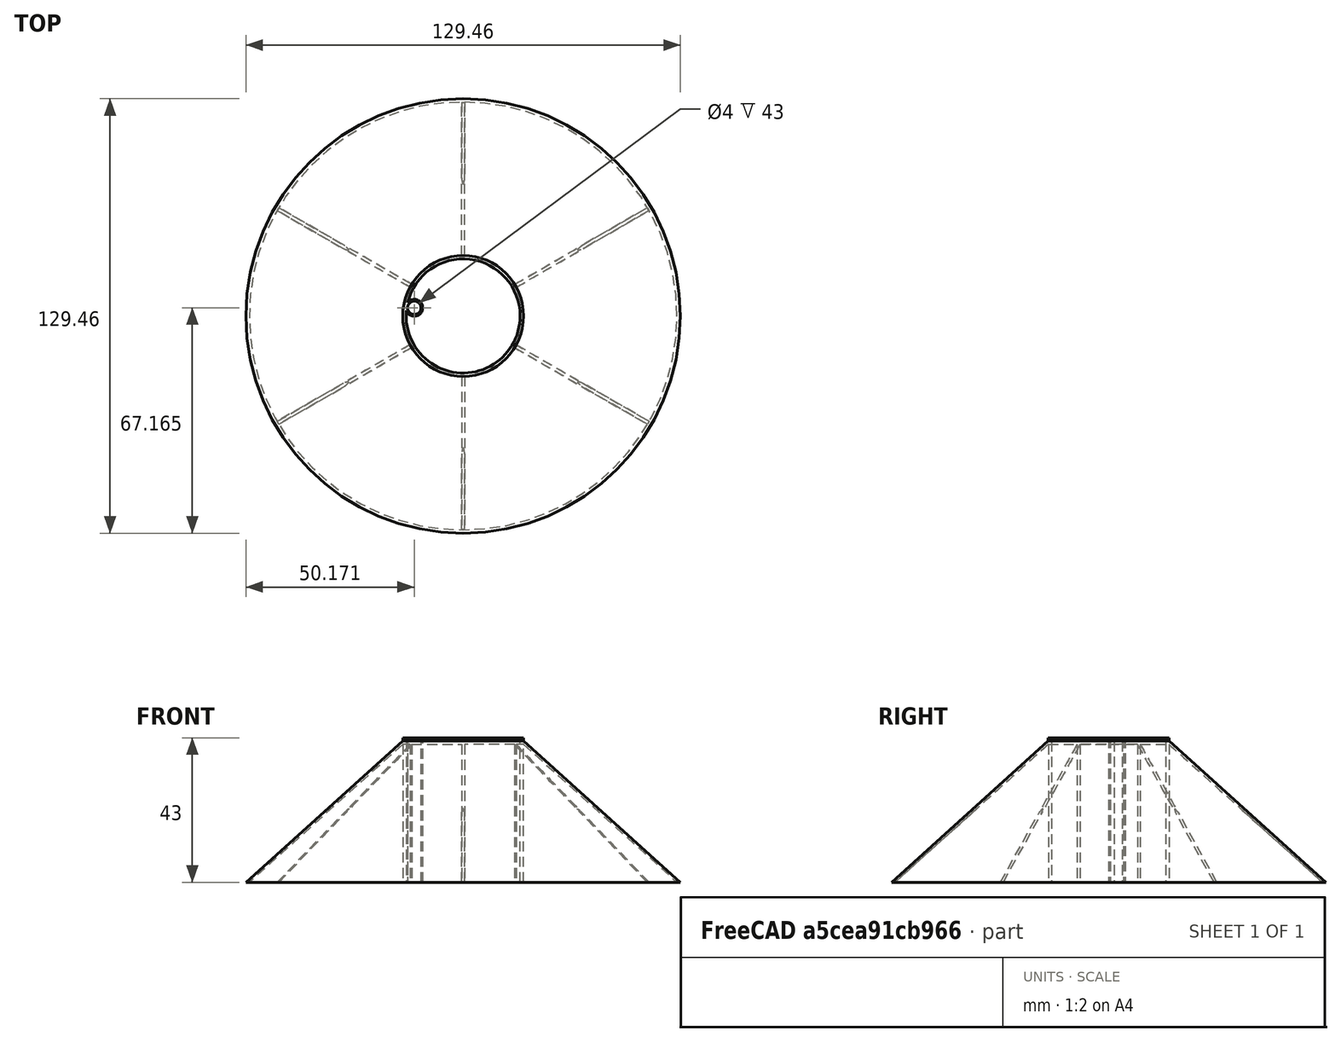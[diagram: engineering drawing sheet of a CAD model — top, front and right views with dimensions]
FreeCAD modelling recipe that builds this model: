
FCSTD DOCUMENT  (FreeCAD 0.20R29603 (Git))
Label: Ez3D-Mini-SaucerX3
License: All rights reserved
LicenseURL: http://en.wikipedia.org/wiki/All_rights_reserved
objects: Sketcher::SketchObject×4, Mesh::Feature×3, PartDesign::Pad×3, PartDesign::PolarPattern×1, PartDesign::Revolution×1, PartDesign::Body×1
note: 14 computed .brp shape members not serialized (recipe doc carries the construction recipe); baked Part::Feature solids carry a one-line shape summary decoded from their .brp

FEATURE [Mesh::Feature] Ez3D_13mmMotorTubeOnly_Body  label="Ez3D-13mmMotorTubeOnly-Body"
  Placement = pos=(-7.5,-5,0) rot=(0,0,1;0rad)
FEATURE [Mesh::Feature] Ez3D_13mmMotorTubeOnly_Body001  label="Ez3D-13mmMotorTubeOnly-Body001"
  Placement = pos=(7.5,-5,0) rot=(0,0,1;0rad)
FEATURE [Sketcher::SketchObject] Sketch  label="Center Support Structure"
  FullyConstrained = true
  MapMode = 5
  Support = -> [XY_Plane]
  sketch-geometry (2):
    g0: Circle CenterX=0 CenterY=0 CenterZ=0 NormalX=0 NormalY=0 NormalZ=1 AngleXU=0 Radius=17
    g1: Circle CenterX=0 CenterY=0 CenterZ=0 NormalX=0 NormalY=0 NormalZ=1 AngleXU=0 Radius=18
  constraints (4):
    c: Coincident(g0,g-1)
    c: Coincident(g1,g0)
    c: Diameter(g0) = 34
    c: Diameter(g1) = 36
FEATURE [PartDesign::Pad] Pad
  Direction = (0,0,1)
  Length = 43
  Length2 = 10
  Profile = -> Sketch
  ReferenceAxis = -> Sketch [N_Axis]
  Type = 0
FEATURE [Sketcher::SketchObject] Sketch001  label=""Fins""
  FullyConstrained = false
  MapMode = 5
  Placement = pos=(0,0,0) rot=(0.57735,0.57735,0.57735;2.0944rad)
  Support = -> [YZ_Plane]
  sketch-geometry (3):
    g0: LineSegment StartX=17 StartY=42 StartZ=0 EndX=17 EndY=0 EndZ=0
    g1: LineSegment StartX=17 StartY=0 StartZ=0 EndX=63.6847 EndY=0 EndZ=0
    g2: LineSegment StartX=63.6847 StartY=0 StartZ=0 EndX=17 EndY=42 EndZ=0
  constraints (8):
    c: Vertical(g0)
    c: Coincident(g0,g1)
    c: PointOnObject(g1,g-1)
    c: Horizontal(g1)
    c: Coincident(g1,g2)
    c: Coincident(g2,g0)
    c: DistanceY(g0,g0) = 42
    c: DistanceX(g-1,g0) = 17
FEATURE [PartDesign::Pad] Pad001
  BaseFeature = -> Pad
  Direction = (1,-2e-16,3e-16)
  Length = 1
  Length2 = 10
  Midplane = true
  Profile = -> Sketch001
  ReferenceAxis = -> Sketch001 [N_Axis]
  Type = 0
FEATURE [PartDesign::PolarPattern] PolarPattern
  Angle = 360
  Axis = -> Z_Axis
  BaseFeature = -> Pad001
  Occurrences = 6
  Originals = -> [Pad001]
FEATURE [Sketcher::SketchObject] Sketch002  label="Top"
  FullyConstrained = false
  MapMode = 5
  Placement = pos=(0,0,0) rot=(0.57735,0.57735,0.57735;2.0944rad)
  Support = -> [YZ_Plane]
  sketch-geometry (4):
    g0: LineSegment StartX=17 StartY=42.9655 StartZ=0 EndX=17 EndY=41.9655 EndZ=0
    g1: LineSegment StartX=17 StartY=41.9655 StartZ=0 EndX=63.7265 EndY=0 EndZ=0
    g2: LineSegment StartX=63.7265 StartY=0 StartZ=0 EndX=64.7265 EndY=0 EndZ=0
    g3: LineSegment StartX=64.7265 StartY=0 StartZ=0 EndX=17 EndY=42.9655 EndZ=0
  constraints (10):
    c: Coincident(g0,g1)
    c: PointOnObject(g1,g-1)
    c: Coincident(g1,g2)
    c: PointOnObject(g2,g-1)
    c: Coincident(g2,g3)
    c: Coincident(g3,g0)
    c: DistanceX(g2,g2) = 1
    c: Vertical(g0)
    c: DistanceY(g0,g0) = 1
    c: DistanceX(g-1,g0) = 17
FEATURE [PartDesign::Revolution] Revolution
  Angle = 360
  Axis = (-2e-16,3e-16,1)
  Base = (0,0,0)
  BaseFeature = -> PolarPattern
  Profile = -> Sketch002
  ReferenceAxis = -> Sketch002 [V_Axis]
  Reversed = true
FEATURE [Sketcher::SketchObject] Sketch003  label="Launch Lug"
  FullyConstrained = false
  MapMode = 5
  Support = -> [XY_Plane]
  sketch-geometry (2):
    g0: Circle CenterX=-14.5594 CenterY=2.43489 CenterZ=0 NormalX=0 NormalY=0 NormalZ=1 AngleXU=0 Radius=2.5
    g1: Circle CenterX=-14.5594 CenterY=2.43489 CenterZ=0 NormalX=0 NormalY=0 NormalZ=1 AngleXU=0 Radius=2
  constraints (3):
    c: Coincident(g1,g0)
    c: Diameter(g0) = 5
    c: Diameter(g1) = 4
FEATURE [PartDesign::Pad] Pad002  label="Launch Lug001"
  BaseFeature = -> Revolution
  Direction = (0,0,1)
  Length = 43
  Length2 = 10
  Profile = -> Sketch003
  ReferenceAxis = -> Sketch003 [N_Axis]
  Type = 0
FEATURE [PartDesign::Body] Body
  Group = -> [Sketch,Pad,Sketch001,Pad001,PolarPattern,Sketch002,Revolution,Sketch003,Pad002]
  Origin = -> Origin
  Tip = -> Pad002
FEATURE [Mesh::Feature] Ez3D_13mmMotorTubeOnly_Body002  label="Ez3D-13mmMotorTubeOnly-Body002"
  Placement = pos=(0,9,0) rot=(0,0,1;0rad)
